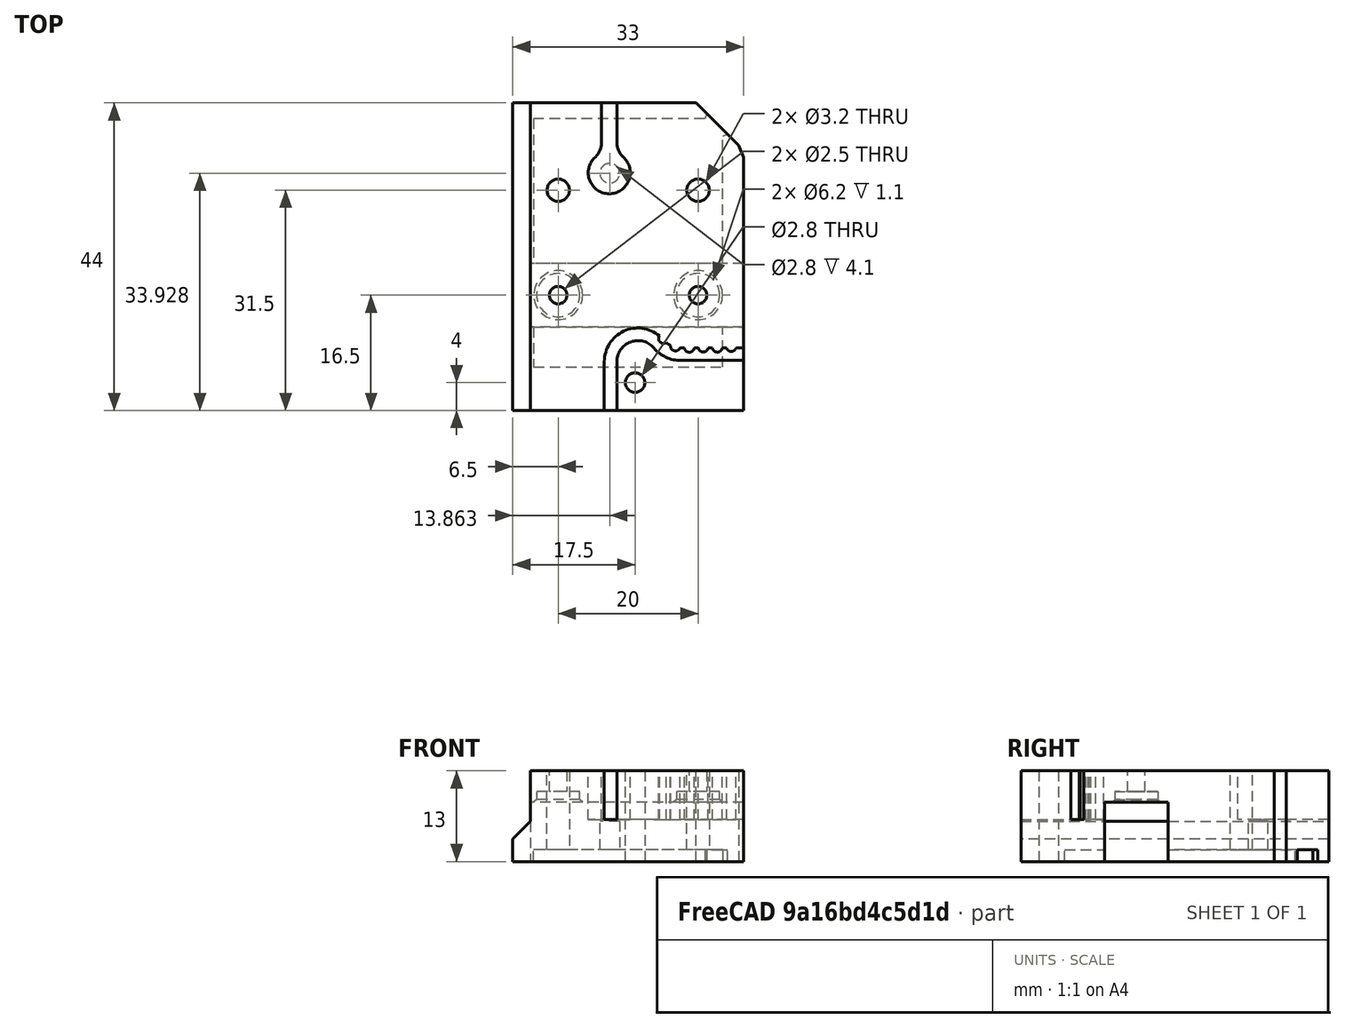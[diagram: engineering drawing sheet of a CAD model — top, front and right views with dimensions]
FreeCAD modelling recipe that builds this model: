
FCSTD DOCUMENT  (FreeCAD 0.19R)
Label: Yjoint_bolted_long
License: All rights reserved
LicenseURL: http://en.wikipedia.org/wiki/All_rights_reserved
objects: Sketcher::SketchObject×12, PartDesign::Pocket×9, PartDesign::Pad×3, PartDesign::Chamfer×3, PartDesign::Body×1, Mesh::Feature×1
note: 43 computed .brp shape members not serialized (recipe doc carries the construction recipe); baked Part::Feature solids carry a one-line shape summary decoded from their .brp

FEATURE [Sketcher::SketchObject] Sketch
  FullyConstrained = false
  MapMode = 5
  Support = -> [XY_Plane]
  sketch-geometry (9):
    g0: LineSegment StartX=-16.5 StartY=20 StartZ=0 EndX=16.5 EndY=20 EndZ=0
    g1: LineSegment StartX=16.5 StartY=20 StartZ=0 EndX=16.5 EndY=-24 EndZ=0
    g2: LineSegment StartX=16.5 StartY=-24 StartZ=0 EndX=-16.5 EndY=-24 EndZ=0
    g3: LineSegment StartX=-16.5 StartY=-24 StartZ=0 EndX=-16.5 EndY=20 EndZ=0
    g4: LineSegment StartX=-37.8866 StartY=-3 StartZ=0 EndX=43.1927 EndY=-3 EndZ=0
    g5: LineSegment StartX=43.1927 StartY=-3 StartZ=0 EndX=43.1927 EndY=-12 EndZ=0
    g6: LineSegment StartX=43.1927 StartY=-12 StartZ=0 EndX=-37.8866 EndY=-12 EndZ=0
    g7: LineSegment StartX=-37.8866 StartY=-12 StartZ=0 EndX=-37.8866 EndY=-3 EndZ=0
    g8: LineSegment StartX=-54.8094 StartY=-7.5 StartZ=0 EndX=51.9088 EndY=-7.5 EndZ=0
  constraints (22):
    c: Coincident(g0,g1)
    c: Coincident(g1,g2)
    c: Coincident(g2,g3)
    c: Coincident(g3,g0)
    c: Horizontal(g2)
    c: Vertical(g1)
    c: Vertical(g3)
    c: Distance(g2) = 33
    c: Coincident(g4,g5)
    c: Coincident(g5,g6)
    c: Coincident(g6,g7)
    c: Coincident(g7,g4)
    c: Horizontal(g4)
    c: Horizontal(g6)
    c: Vertical(g5)
    c: Vertical(g7)
    c: Symmetric(g5,g4,g8)
    c: DistanceY(g8) = -7.5
    c: Distance(g5) = 9
    c: Distance(g0,g4) = 23
    c: Symmetric(g0,g0,g-2)
    c: DistanceY(g1) = -24
FEATURE [PartDesign::Pad] Pad
  Direction = (1,1,1)
  Length = 13
  Length2 = 100
  Profile = -> Sketch
  Type = 0
FEATURE [Sketcher::SketchObject] Sketch001  label="beltreleif"
  FullyConstrained = false
  MapMode = 5
  Placement = pos=(0,-24,0) rot=(1,0,0;1.5708rad)
  Support = -> [Pad]
  sketch-geometry (3):
    g0: LineSegment StartX=-23.7076 StartY=-3.95758 StartZ=0 EndX=-14 EndY=5.75 EndZ=0
    g1: LineSegment StartX=-14 StartY=5.75 StartZ=0 EndX=-14 EndY=31.0099 EndZ=0
    g2: LineSegment StartX=-14 StartY=31.0099 StartZ=0 EndX=-23.7076 EndY=-3.95758 EndZ=0
  constraints (8):
    c: Coincident(g0,g1)
    c: Vertical(g1)
    c: Coincident(g1,g2)
    c: Coincident(g2,g0)
    c: Angle(g0) = 0.785398
    c: DistanceX(g0) = -14
    c: Distance(g2) = 36.29
    c: DistanceY(g0) = 5.75
FEATURE [PartDesign::Pocket] Pocket
  BaseFeature = -> Pad
  Length = 5
  Length2 = 100
  Profile = -> Sketch001
  Type = 1
FEATURE [Sketcher::SketchObject] Sketch002  label="RailPocket"
  FullyConstrained = false
  MapMode = 5
  Placement = pos=(16.5,0,0) rot=(0.57735,0.57735,0.57735;2.0944rad)
  Support = -> [Pocket]
  sketch-geometry (5):
    g0: LineSegment StartX=-12.05 StartY=8.5 StartZ=0 EndX=-2.95 EndY=8.5 EndZ=0
    g1: LineSegment StartX=-2.95 StartY=8.5 StartZ=0 EndX=-2.95 EndY=-7.81784 EndZ=0
    g2: LineSegment StartX=-2.95 StartY=-7.81784 StartZ=0 EndX=-12.05 EndY=-7.81784 EndZ=0
    g3: LineSegment StartX=-12.05 StartY=-7.81784 StartZ=0 EndX=-12.05 EndY=8.5 EndZ=0
    g4: LineSegment StartX=-7.5 StartY=9.53875 StartZ=0 EndX=-7.5 EndY=-20.3605 EndZ=0
  constraints (12):
    c: Coincident(g0,g1)
    c: Coincident(g1,g2)
    c: Coincident(g2,g3)
    c: Coincident(g3,g0)
    c: Horizontal(g0)
    c: Horizontal(g2)
    c: Vertical(g1)
    c: Vertical(g3)
    c: Distance(g0) = 9.1
    c: Symmetric(g0,g0,g4)
    c: DistanceX(g4) = -7.5
    c: DistanceY(g0) = 8.5
FEATURE [PartDesign::Pocket] Pocket001
  BaseFeature = -> Pocket
  Length = 30.5
  Length2 = 100
  Profile = -> Sketch002
  Type = 0
FEATURE [Sketcher::SketchObject] Sketch003  label="CarriageBolts"
  FullyConstrained = true
  MapMode = 5
  Placement = pos=(0,0,13) rot=(0,0,1;0rad)
  Support = -> [Pocket001]
  sketch-geometry (4):
    g0: Circle CenterX=10 CenterY=7.5 CenterZ=0 NormalX=0 NormalY=0 NormalZ=1 AngleXU=0 Radius=1.6
    g1: Circle CenterX=-10 CenterY=7.5 CenterZ=0 NormalX=0 NormalY=0 NormalZ=1 AngleXU=0 Radius=1.6
    g2: Circle CenterX=-10 CenterY=-7.5 CenterZ=0 NormalX=0 NormalY=0 NormalZ=1 AngleXU=0 Radius=1.25
    g3: Circle CenterX=10 CenterY=-7.5 CenterZ=0 NormalX=0 NormalY=0 NormalZ=1 AngleXU=0 Radius=1.25
  constraints (9):
    c: DistanceY(g0) = 7.5
    c: DistanceX(g0) = 10
    c: Symmetric(g1,g0,g-2)
    c: Symmetric(g0,g2,g-1)
    c: Symmetric(g1,g3,g-1)
    c: Diameter(g1) = 3.2
    c: Equal(g1,g0)
    c: Diameter(g3) = 2.5
    c: Equal(g3,g2)
FEATURE [PartDesign::Pocket] Pocket002
  BaseFeature = -> Pocket001
  Length = 5
  Length2 = 100
  Profile = -> Sketch003
  Type = 1
FEATURE [Sketcher::SketchObject] Sketch004  label="MotorSideBeltClamp"
  FullyConstrained = false
  MapMode = 5
  Placement = pos=(0,0,13) rot=(0,0,1;0rad)
  Support = -> [Pocket002]
  sketch-geometry (13):
    g0: LineSegment StartX=-3.8 StartY=-19.337 StartZ=0 EndX=-3.8 EndY=-36 EndZ=0
    g1: LineSegment StartX=-3.8 StartY=-36 StartZ=0 EndX=-1.6 EndY=-36 EndZ=0
    g2: LineSegment StartX=-1.6 StartY=-36 StartZ=0 EndX=-1.6 EndY=-19.337 EndZ=0
    g3: ArcOfCircle CenterX=-2.7 CenterY=-15 CenterZ=0 NormalX=0 NormalY=0 NormalZ=1 AngleXU=0 Radius=3 StartAngle=5.45738 EndAngle=10.2506
    g4: ArcOfCircle CenterX=1.3 CenterY=-19.337 CenterZ=0 NormalX=0 NormalY=0 NormalZ=1 AngleXU=0 Radius=2.9 StartAngle=2.31579 EndAngle=3.14159
    g5: ArcOfCircle CenterX=-6.7 CenterY=-19.337 CenterZ=0 NormalX=0 NormalY=0 NormalZ=1 AngleXU=0 Radius=2.9 StartAngle=6e-16 EndAngle=0.825804
    g6: LineSegment StartX=-2.7 StartY=-15 StartZ=0 EndX=-2.7 EndY=-40.8271 EndZ=0
    g7: LineSegment StartX=-3.8 StartY=23.44 StartZ=0 EndX=-1.6 EndY=23.44 EndZ=0
    g8: LineSegment StartX=-1.6 StartY=23.44 StartZ=0 EndX=-1.6 EndY=14.337 EndZ=0
    g9: LineSegment StartX=-3.8 StartY=23.44 StartZ=0 EndX=-3.8 EndY=14.337 EndZ=0
    g10: ArcOfCircle CenterX=-2.7 CenterY=10 CenterZ=0 NormalX=0 NormalY=0 NormalZ=1 AngleXU=0 Radius=3 StartAngle=2.31579 EndAngle=7.10899
    g11: ArcOfCircle CenterX=1.3 CenterY=14.337 CenterZ=0 NormalX=0 NormalY=0 NormalZ=1 AngleXU=0 Radius=2.9 StartAngle=3.14159 EndAngle=3.9674
    g12: ArcOfCircle CenterX=-6.7 CenterY=14.337 CenterZ=0 NormalX=0 NormalY=0 NormalZ=1 AngleXU=0 Radius=2.9 StartAngle=5.45738 EndAngle=6.28319
  constraints (32):
    c: Vertical(g0)
    c: Coincident(g0,g1)
    c: Horizontal(g1)
    c: Coincident(g1,g2)
    c: Tangent(g4,g3) = 1.5708
    c: Tangent(g4,g2) = 1.5708
    c: Tangent(g5,g3) = 1.5708
    c: Tangent(g5,g0) = 1.5708
    c: Coincident(g6,g3)
    c: Symmetric(g1,g0,g6)
    c: Symmetric(g2,g0,g6)
    c: DistanceX(g3) = -2.7
    c: Diameter(g3) = 6
    c: Distance(g4,g5) = 8
    c: Distance(g1) = 2.2
    c: DistanceY(g3) = -15
    c: DistanceY(g1) = -36
    c: Coincident(g7,g8)
    c: Vertical(g8)
    c: Coincident(g7,g9)
    c: Tangent(g11,g10) = 1.5708
    c: Diameter(g10) = 6
    c: Tangent(g11,g8) = -1.5708
    c: Tangent(g12,g10) = 1.5708
    c: Tangent(g12,g9) = 1.5708
    c: Symmetric(g7,g7,g6)
    c: Distance(g7) = 2.2
    c: PointOnObject(g10,g6)
    c: Symmetric(g8,g9,g6)
    c: Distance(g11,g12) = 8
    c: DistanceY(g10) = 10
    c: DistanceY(g7) = 23.44
FEATURE [PartDesign::Pocket] Pocket003
  BaseFeature = -> Pocket002
  Length = 7
  Length2 = 100
  Profile = -> Sketch004
  Type = 0
FEATURE [Sketcher::SketchObject] Sketch005  label="BottomPocket"
  FullyConstrained = true
  MapMode = 5
  Placement = pos=(0,0,0) rot=(1,0,0;3.14159rad)
  Support = -> [Pocket003]
  sketch-geometry (4):
    g0: LineSegment StartX=-13.5 StartY=17.75 StartZ=0 EndX=13.5 EndY=17.75 EndZ=0
    g1: LineSegment StartX=13.5 StartY=17.75 StartZ=0 EndX=13.5 EndY=-17.75 EndZ=0
    g2: LineSegment StartX=13.5 StartY=-17.75 StartZ=0 EndX=-13.5 EndY=-17.75 EndZ=0
    g3: LineSegment StartX=-13.5 StartY=-17.75 StartZ=0 EndX=-13.5 EndY=17.75 EndZ=0
  constraints (11):
    c: Coincident(g0,g1)
    c: Coincident(g1,g2)
    c: Coincident(g2,g3)
    c: Coincident(g3,g0)
    c: Horizontal(g2)
    c: Vertical(g1)
    c: Vertical(g3)
    c: Distance(g0) = 27
    c: Distance(g1) = 35.5
    c: Symmetric(g0,g2,g-1)
    c: Horizontal(g0)
FEATURE [PartDesign::Pocket] Pocket004
  BaseFeature = -> Pocket003
  Length = 1.7
  Length2 = 100
  Profile = -> Sketch005
  Type = 0
FEATURE [Sketcher::SketchObject] Sketch006  label="CornerClip"
  FullyConstrained = false
  MapMode = 5
  Placement = pos=(0,0,13) rot=(0,0,1;0rad)
  Support = -> [Pocket004]
  sketch-geometry (3):
    g0: LineSegment StartX=1.0446 StartY=28.6539 StartZ=0 EndX=17.0625 EndY=12.636 EndZ=0
    g1: LineSegment StartX=17.0625 StartY=12.636 StartZ=0 EndX=17.0625 EndY=28.6539 EndZ=0
    g2: LineSegment StartX=17.0625 StartY=28.6539 StartZ=0 EndX=1.0446 EndY=28.6539 EndZ=0
  constraints (7):
    c: Coincident(g0,g1)
    c: Vertical(g1)
    c: Coincident(g1,g2)
    c: Horizontal(g2)
    c: Coincident(g0,g2)
    c: Angle(g0) = -0.785398
    c: Distance(g-1,g0) = 21
FEATURE [PartDesign::Pocket] Pocket005
  BaseFeature = -> Pocket004
  Length = 5
  Length2 = 100
  Profile = -> Sketch006
  Type = 1
FEATURE [Sketcher::SketchObject] Sketch007  label="clampHole"
  ExternalGeometry = -> [Pocket005]
  FullyConstrained = false
  MapMode = 5
  Placement = pos=(0,0,13) rot=(0,0,1;0rad)
  Support = -> [Pocket005]
  sketch-geometry (2):
    g0: Circle CenterX=-2.63724 CenterY=9.92805 CenterZ=0 NormalX=0 NormalY=0 NormalZ=1 AngleXU=0 Radius=1.4
    g1: Circle CenterX=1 CenterY=-20 CenterZ=0 NormalX=0 NormalY=0 NormalZ=1 AngleXU=0 Radius=1.4
  constraints (4):
    c: Diameter(g0) = 2.8
    c: Diameter(g1) = 2.8
    c: DistanceY(g1) = -20
    c: DistanceX(g1) = 1
FEATURE [Sketcher::SketchObject] Sketch008  label="printFilm"
  FullyConstrained = false
  MapMode = 5
  Placement = pos=(0,0,6) rot=(0,0,1;0rad)
  sketch-geometry (8):
    g0: LineSegment StartX=-7.42355 StartY=14.214 StartZ=0 EndX=2.97442 EndY=14.214 EndZ=0
    g1: LineSegment StartX=2.97442 StartY=14.214 StartZ=0 EndX=2.97442 EndY=6.02841 EndZ=0
    g2: LineSegment StartX=2.97442 StartY=6.02841 StartZ=0 EndX=-7.42355 EndY=6.02841 EndZ=0
    g3: LineSegment StartX=-7.42355 StartY=6.02841 StartZ=0 EndX=-7.42355 EndY=14.214 EndZ=0
    g4: LineSegment StartX=-5.77868 StartY=-12.14 StartZ=0 EndX=6.57401 EndY=-12.14 EndZ=0
    g5: LineSegment StartX=6.57401 StartY=-12.14 StartZ=0 EndX=6.57401 EndY=-18.374 EndZ=0
    g6: LineSegment StartX=6.57401 StartY=-18.374 StartZ=0 EndX=-5.77868 EndY=-18.374 EndZ=0
    g7: LineSegment StartX=-5.77868 StartY=-18.374 StartZ=0 EndX=-5.77868 EndY=-12.14 EndZ=0
  constraints (16):
    c: Coincident(g0,g1)
    c: Coincident(g1,g2)
    c: Coincident(g2,g3)
    c: Coincident(g3,g0)
    c: Horizontal(g0)
    c: Horizontal(g2)
    c: Vertical(g1)
    c: Vertical(g3)
    c: Coincident(g4,g5)
    c: Coincident(g5,g6)
    c: Coincident(g6,g7)
    c: Coincident(g7,g4)
    c: Horizontal(g4)
    c: Horizontal(g6)
    c: Vertical(g5)
    c: Vertical(g7)
FEATURE [Sketcher::SketchObject] Sketch009  label="BeltTrap1"
  FullyConstrained = true
  MapMode = 5
  Placement = pos=(0,0,13) rot=(0,0,1;0rad)
  sketch-geometry (12):
    g0: ArcOfCircle CenterX=1.4 CenterY=-17 CenterZ=0 NormalX=0 NormalY=0 NormalZ=1 AngleXU=0 Radius=3 StartAngle=0.70304 EndAngle=3.14159
    g1: ArcOfCircle CenterX=1.4 CenterY=-17 CenterZ=0 NormalX=0 NormalY=0 NormalZ=1 AngleXU=0 Radius=4.8 StartAngle=0.70304 EndAngle=3.14159
    g2: LineSegment StartX=-3.4 StartY=-17 StartZ=0 EndX=-1.6 EndY=-17 EndZ=0
    g3: LineSegment StartX=-1.6 StartY=-17 StartZ=0 EndX=-1.6 EndY=-27 EndZ=0
    g4: LineSegment StartX=-1.6 StartY=-27 StartZ=0 EndX=-3.4 EndY=-27 EndZ=0
    g5: LineSegment StartX=-3.4 StartY=-27 StartZ=0 EndX=-3.4 EndY=-17 EndZ=0
    g6: LineSegment StartX=-4.78 StartY=-17 StartZ=0 EndX=6 EndY=-17 EndZ=0
    g7: ArcOfCircle CenterX=7.5411 CenterY=-11.7954 CenterZ=0 NormalX=0 NormalY=0 NormalZ=1 AngleXU=0 Radius=3.24989 StartAngle=3.84463 EndAngle=4.71239
    g8: ArcOfCircle CenterX=7.5411 CenterY=-11.7954 CenterZ=0 NormalX=0 NormalY=0 NormalZ=1 AngleXU=0 Radius=5.04989 StartAngle=3.84463 EndAngle=4.71239
    g9: LineSegment StartX=21.71 StartY=-15.0453 StartZ=0 EndX=7.5411 EndY=-15.0453 EndZ=0
    g10: LineSegment StartX=21.71 StartY=-16.8453 StartZ=0 EndX=7.5411 EndY=-16.8453 EndZ=0
    g11: LineSegment StartX=21.71 StartY=-15.0453 StartZ=0 EndX=21.71 EndY=-16.8453 EndZ=0
  constraints (34):
    c: Coincident(g1,g0)
    c: Distance(g0,g0) = 3
    c: DistanceX(g0) = 1.4
    c: Coincident(g2,g1)
    c: Coincident(g2,g0)
    c: Tangent(g0,g3) = -1.5708
    c: Coincident(g3,g4)
    c: Horizontal(g4)
    c: Coincident(g4,g5)
    c: Coincident(g5,g1)
    c: Vertical(g5)
    c: Distance(g4) = 1.8
    c: Distance(g3) = 10
    c: Horizontal(g6)
    c: PointOnObject(g0,g6)
    c: PointOnObject(g1,g6)
    c: Parallel(g3,g5)
    c: DistanceY(g6) = -17
    c: Distance(g6) = 10.78
    c: DistanceX(g6) = -4.78
    c: Coincident(g8,g7)
    c: Tangent(g7,g1) = 1.5708
    c: Tangent(g8,g0) = 1.5708
    c: Tangent(g7,g9) = 1.5708
    c: Coincident(g7,g9)
    c: Tangent(g8,g10) = 1.5708
    c: Parallel(g10,g9)
    c: Horizontal(g9)
    c: Coincident(g11,g9)
    c: Coincident(g11,g10)
    c: Vertical(g11)
    c: DistanceX(g9) = 21.71
    c: DistanceX(g8) = 7.5411
    c: DistanceY(g8) = -16.8453
FEATURE [Sketcher::SketchObject] Sketch010  label="chain"
  FullyConstrained = false
  MapMode = 5
  Placement = pos=(0,0,13) rot=(0,0,1;0rad)
  sketch-geometry (6):
    g0: Circle CenterX=5.06388 CenterY=-13.7081 CenterZ=0 NormalX=0 NormalY=0 NormalZ=1 AngleXU=0 Radius=0.7
    g1: Circle CenterX=6.75695 CenterY=-14.7728 CenterZ=0 NormalX=0 NormalY=0 NormalZ=1 AngleXU=0 Radius=0.7
    g2: Circle CenterX=8.74722 CenterY=-14.9698 CenterZ=0 NormalX=0 NormalY=0 NormalZ=1 AngleXU=0 Radius=0.7
    g3: Circle CenterX=10.7469 CenterY=-14.9346 CenterZ=0 NormalX=0 NormalY=0 NormalZ=1 AngleXU=0 Radius=0.7
    g4: Circle CenterX=12.7468 CenterY=-14.9525 CenterZ=0 NormalX=0 NormalY=0 NormalZ=1 AngleXU=0 Radius=0.7
    g5: Circle CenterX=14.7446 CenterY=-14.8585 CenterZ=0 NormalX=0 NormalY=0 NormalZ=1 AngleXU=0 Radius=0.7
  constraints (5):
    c: Distance(g0,g1) = 2
    c: Distance(g1,g2) = 2
    c: Distance(g3,g4) = 2
    c: Distance(g3,g2) = 2
    c: Distance(g5,g4) = 2
FEATURE [PartDesign::Pocket] Pocket006
  BaseFeature = -> Pocket005
  Length = 5
  Length2 = 100
  Profile = -> Sketch007
  Type = 1
FEATURE [PartDesign::Pad] Pad001
  BaseFeature = -> Pocket006
  Direction = (1,1,1)
  Length = 0.2
  Length2 = 100
  Profile = -> Sketch008
  Reversed = true
  Type = 0
FEATURE [PartDesign::Pocket] Pocket007
  BaseFeature = -> Pad001
  Length = 7
  Length2 = 100
  Profile = -> Sketch009
  Type = 0
FEATURE [PartDesign::Pad] Pad002
  BaseFeature = -> Pocket007
  Direction = (1,1,1)
  Length = 8
  Length2 = 100
  Profile = -> Sketch010
  Reversed = true
  Type = 0
FEATURE [Sketcher::SketchObject] Sketch012
  FullyConstrained = true
  MapMode = 5
  Placement = pos=(0,0,8.5) rot=(1,0,0;3.14159rad)
  sketch-geometry (2):
    g0: Circle CenterX=10 CenterY=7.5 CenterZ=0 NormalX=0 NormalY=0 NormalZ=1 AngleXU=0 Radius=3.1
    g1: Circle CenterX=-10 CenterY=7.5 CenterZ=0 NormalX=0 NormalY=0 NormalZ=1 AngleXU=0 Radius=3.1
  constraints (6):
    c: Diameter(g0) = 6.2
    c: Equal(g0,g1)
    c: DistanceY(g1) = 7.5
    c: DistanceY(g0) = 7.5
    c: DistanceX(g1) = -10
    c: DistanceX(g0) = 10
FEATURE [PartDesign::Pocket] Pocket008
  BaseFeature = -> Pad002
  Length = 1.5
  Length2 = 100
  Profile = -> Sketch012
  Type = 0
FEATURE [PartDesign::Chamfer] Chamfer
  Angle = 45
  Base = -> Pocket008 [Edge26,Edge28]
  BaseFeature = -> Pocket008
  ChamferType = 0
  FlipDirection = false
  Size = 1
  Size2 = 1
  SupportTransform = false
FEATURE [PartDesign::Chamfer] Chamfer001
  Angle = 45
  Base = -> Chamfer [Edge170,Edge171]
  BaseFeature = -> Chamfer
  ChamferType = 0
  FlipDirection = false
  Size = 0.4
  Size2 = 1
  SupportTransform = false
FEATURE [PartDesign::Chamfer] Chamfer002
  Angle = 45
  Base = -> Chamfer001 [Edge154]
  BaseFeature = -> Chamfer001
  ChamferType = 0
  FlipDirection = false
  Size = 1
  Size2 = 1
  SupportTransform = false
FEATURE [PartDesign::Body] Body
  Group = -> [Sketch,Pad,Sketch001,Pocket,Sketch002,Pocket001,Sketch003,Pocket002,Sketch004,Pocket003,Sketch005,Pocket004,Sketch006,Pocket005,Sketch007,Sketch008,Sketch009,Sketch010,Pocket006,Pad001,Pocket007,Pad002,Sketch012,Pocket008,Chamfer,Chamfer001,Chamfer002]
  Origin = -> Origin
  Tip = -> Chamfer002
FEATURE [Mesh::Feature] Mesh  label="Chamfer002 (Meshed)"
